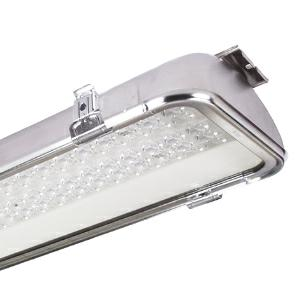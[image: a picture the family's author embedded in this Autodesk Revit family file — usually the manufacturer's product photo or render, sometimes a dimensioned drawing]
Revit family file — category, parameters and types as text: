
# Revit family: 3f_filippi_-_beta_235_93_vt_ampio_3f_filippi_-_52877_-_beta_235_led_931x50_ampio_vt_l1265
name_source: partatom
category: Lighting Fixtures
units: mm (PartAtom-declared; Revit-internal decimal feet)

## family parameters
Cut with Voids When Loaded = No
Host = Face
Light Source = No
Part Type = Normal
Room Calculation Point = No
Round Connector Dimension = Use Diameter
Shared = No

## types (1)
- 3F Filippi - Beta 235 93 VT Ampio (1 x LED, 8229 lm, 54 W, 4000 K)
    Apparent Load = 54 VA
    Approval mark = CE
    CIE Flux Codes = 56 92 99 100 100
    Color Rendering = 80
    Color Temperature = 4000 K
    Control Gear = Electronic ballast
    Default Elevation = 1800 mm
    Description = ILLUMINOTECHNICAL
Luminous efficiency 100% (DLOR 100%, ULOR 0%).
Initial luminous flux of the luminaire 8229 lm.
Wide symmetric distribution.
Installation Interdistance Transv.D = 1.19 x hu - Long.D = 1.18 x hu.
Tabular UGR (CIE 117 - 4H-8H; S=0.25H; 70/50/20): RUG 20.2 - 21.8.
Beam angle: 99° - 105°.
Luminous efficacy 152 lm/W.
Lifetime (L93/B10): 30000 h. (tq+25°C)
Lifetime (L90/B10): 50000 h. (tq+25°C)
Lifetime (L85/B10): 80000 h. (tq+25°C)
Lifetime (L80/B10): 100000 h. (tq+25°C)
Lifetime (L85/B10): 50000 h. (tq+45°C)
Sudden decreased luminous flux after 50000 hours: 0% (C0).
Photobiological safety in compliance with IEC/TR 62778: RG0 risk exempt, (IEC 62471).
In compliance with IEC/EN 62722-2-1 - IEC/EN 62717 standards.

SOURCE
Linear LED module 50W/840.
Energy efficiency class (UE 2019/2020 - UE 2019/2015): C.
CIE 13.3 Colour rendering index: CRI >80 (R9 <50%).
IES TM-30 Fidelity Index: Rf = 84 Rg = 95.
CCT nominal colour temperature 4000 K.
Colour initial tolerance (MacAdam): SDCM 3.

MECHANICAL
Housing in AISI 304 stainless steel, pressed in one single piece.
VT transparent glass, non-combustible, single-piece perimeter frame in stainless steel.
Oversized gear-tray reflector unit in highly reflective white painted hot-galvanised steel.
Methacrylate (PMMA) lenses with external flat surface.
Stainless steel snap-lock clips for diffuser mounting (safety n° 4 per fixture).
Luminaire with limited surface temperature. - D - (EN 60598-2-24)
Dimensions: 1265x235 mm, height 105 mm. Weight 8.67 kg.
IP65 protection degree.
Mechanical strength to impacts IK09 (10 joule).
Glow-wire test resistance 960°C.

ELECTRICAL
Halogen Free electronic wiring 230V-50/60Hz, power factor 0.95, THD <25%, constant output current, class I, 1 driver.
Power of the luminaire 54 W.
ENEC - CE.
Flicker: <4%.
Luminaire compliant with EN 60598-2-22 for power supply from a centralised emergency system CPSS (Central Power Supply System), not incorporated in the luminaire - high risk areas excluded. The default power and flux are 100% in AC and 100% in DC.
Ambient temperature from -20°C to +45°C.
Temperature class T6 max 85°C.
Quick connection via M20 3P connector with 9-13 mm tightening range.
Relative humidity UR: <85%.

INSTALLATION
Ceiling / Suspended / Wall.
All accessories dedicated to this product are available on the Catalog and on our website www.3F-Filippi.com.

APPLICATIONS
Dry, dusty indoor environments, subject to occasional water splashes.
Any environments except the ones where the luminaire materials are unsuitable.
Industrial environments, warehouses, environments where security locks are required on all clips, e.g. prisons (on request).
Environments in which it is necessary a total protection against falling fragments (eg environments with foodstuffs or machines with moving parts or with extreme temperature changes), use luminaires with laminated glass.
Tempered glass is not immune to falling fragments from harmless and caused by shocks or exceptionally derived from the tempering process.

WARNING
Fixture not suitable for cold stores with an ambient temperature <0°C and/or relative humidity >85%.
Luminaire designed for disposal/recycling at end-of-life.
Replaceable (LED only) light source by a professional. Replaceable control gear by a professional.
    Height = 105 mm
    Lamp = 1 x LED
    Lamp Light Flux = 8229 lm
    Lamp Power = 54 W
    Lamp count = 1
    Length = 1265 mm
    Lifetime = 50000 h
    Luminous efficacy = 152 lm/W
    Manufacturer = 3F Filippi
    ModVariant = No
    Model = 3F Filippi - 52877 - Beta 235 LED 931x50 AMPIO VT L1265
    Mounting Place = Ceiling
    Mounting Type = Pendant
    Number of Poles = 1
    OnlyDefault = Yes
    Power Factor = 1
    Product Name = 3F Filippi - Beta 235 93 VT Ampio
    Product group = pendant luminaire
    ProductGroupID = 9
    Protection Class = Protection class I
    Protection Degree = IP 65
    RLX_Detail_Level = 1
    RLX_Emergency_Light_Flux = 0 lm
    RLX_Emergency_Type = 0
    RLX_Emergency_Type_DB = No
    RlxData = <blob elided: 89561 chars, md5=e1f8ea7a>
    Socket = socket
    Standby Power = 0 W
    System Light Flux = 8229 lm
    System Power = 54 W
    Type Comments = Product without accessories
    Type Image = 3ffilippi_52877.jpg
    URL = http://relux.com
    VarID = ---
    Voltage = 0 V
    Weight = 0.00 kg
    Width = 235 mm

## geometry (parser evidence)
native form markers: Blend x4, Sweep x10
no freeform markers — native parametric forms only
